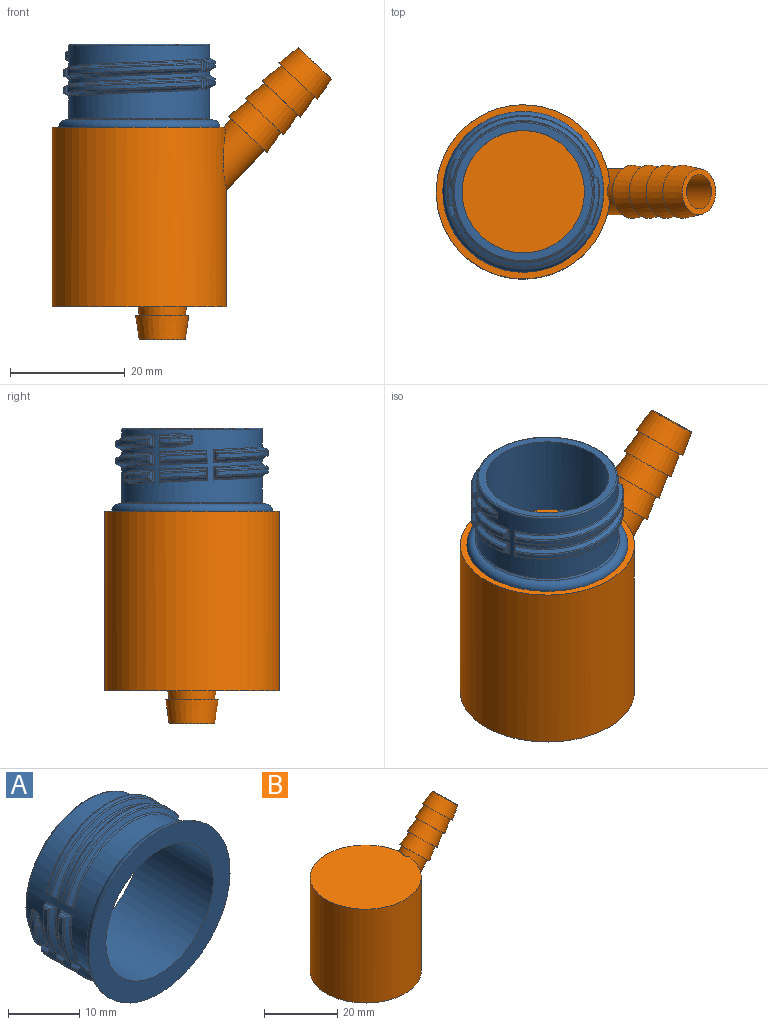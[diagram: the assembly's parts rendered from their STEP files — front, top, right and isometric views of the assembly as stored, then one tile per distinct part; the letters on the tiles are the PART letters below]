
ASSEMBLY  parts=2 mates=1
PART A: 180 faces, bbox 30.3x14.4x30.3 mm
  f0: cylinder r=0.25mm len=2.31mm, axis (0,-1,0), area 0.7mm2, adj f3,f34,f72,f106,f123,f140
  f1: bspline ~22.39x8.9mm, area 7.7mm2, adj f2,f27,f34,f151
  f2: cylinder r=0.25mm len=2.31mm, axis (0,-1,0), area 0.7mm2, adj f1,f27,f28,f32,f34,f175
  f3: bspline ~22.39x8.9mm, area 7.7mm2, adj f0,f34,f123,f124
  f4: bspline ~2.01x0.9mm, area 0.5mm2, adj f5,f31,f34,f50,f51,f139
  f5: plane 1.1x0.46mm, normal (0.06,0.88,-0.48), area 0.2mm2, adj f4,f6,f172
  f6: bspline ~1.83x0.7mm, area 0.8mm2, adj f5,f7,f35,f49,f50
  f7: bspline ~0.63x0.3mm, area 0.1mm2, adj f6,f29,f49,f105
  f8: bspline ~0.83x0.44mm, area 0.3mm2, adj f9,f10,f65,f99
  f9: bspline ~2.12x0.78mm, area 0.5mm2, adj f8,f10,f34,f60,f61,f90
  f10: bspline ~0.31x0.29mm, area 0mm2, adj f8,f9,f121
  f11: bspline ~3.72x1.35mm, area 1mm2, adj f15,f34,f93,f166
  f12: bspline ~2.11x0.63mm, area 0.5mm2, adj f13,f14,f34,f93,f153,f161
  f13: plane 1.04x0.34mm, normal (-0.43,0.89,0.14), area 0.2mm2, adj f12,f48,f114
  f14: cylinder r=0.48mm len=0.13mm, axis (0.89,0.45,-0.06), area 0mm2, adj f12,f15,f93,f114
  f15: bspline ~4.62x2.22mm, area 2.8mm2, adj f11,f14,f70,f75,f95,f114,f117,f119
  f16: bspline ~10.2x2.57mm, area 6.7mm2, adj f38,f45,f83,f86,f92,f96,f115,f149
  f17: bspline ~4.61x2.22mm, area 2.8mm2, adj f61,f62,f64,f70,f102,f119,f138,f163
  f18: bspline ~10.2x2.57mm, area 6.7mm2, adj f38,f73,f83,f86,f96,f115,f149,f170
  f19: cylinder r=13.25mm len=7.77mm, axis (0,-1,0), area 5.5mm2, adj f37,f84,f91,f176
  f20: cylinder r=13.25mm len=23.24mm, axis (0,-1,0), area 19.9mm2, adj f44,f148,f152,f167
  f21: cylinder r=13.25mm len=7.77mm, axis (0,-1,0), area 5.5mm2, adj f38,f45,f83,f170
  f22: cylinder r=13.25mm len=23.24mm, axis (0,-1,0), area 19.9mm2, adj f47,f111,f125,f126
  f23: cylinder r=13.25mm len=7.77mm, axis (0,-1,0), area 5.5mm2, adj f42,f43,f77,f81
  f24: bspline ~10.2x2.57mm, area 6.7mm2, adj f41,f97,f100,f147,f155,f159,f162,f179
  f25: bspline ~25.54x12.83mm, area 22.9mm2, adj f39,f46,f78,f108,f110,f122,f142,f171
  f26: bspline ~10.2x2.57mm, area 6.7mm2, adj f37,f91,f103,f120,f137,f156,f157,f176
  f27: bspline ~25.54x12.83mm, area 22.9mm2, adj f1,f2,f47,f111,f126,f151,f154,f175
  f28: bspline ~25.54x12.82mm, area 22.9mm2, adj f2,f32,f111,f125,f126,f151,f154,f175
  f29: bspline ~6.3x5.77mm, area 5mm2, adj f7,f36,f68,f89,f105,f139,f143,f172
  f30: bspline ~2x0.91mm, area 0.5mm2, adj f34,f52,f53,f58,f59,f136
  f31: bspline ~0.24x0.15mm, area 0mm2, adj f4,f139,f173
  f32: bspline ~22.25x8.69mm, area 7.7mm2, adj f2,f28,f34,f151
  f33: cylinder r=0.25mm len=2.31mm, axis (0,-1,0), area 0.7mm2, adj f34,f76,f94,f101,f116,f177
  f34: cylinder r=12.25mm len=24.5mm, axis (0,-1,0), area 606.8mm2, adj f0,f1,f2,f3,f4,f9,f11,f12
  f35: cylinder r=5mm len=3.78mm, axis (0,-1,0), area 2.6mm2, adj f6,f50,f53,f54,f69,f85,f105,f135
  f36: cylinder r=0.25mm len=1.21mm, axis (0,1,0), area 0.3mm2, adj f29,f79,f89,f135,f143,f165
  f37: cylinder r=0.25mm len=1.21mm, axis (0,-1,0), area 0.3mm2, adj f19,f26,f84,f98,f103,f176
  f38: cylinder r=0.25mm len=1.21mm, axis (0,-1,0), area 0.3mm2, adj f16,f18,f21,f45,f86,f170
  f39: cylinder r=0.25mm len=1.21mm, axis (0,-1,0), area 0.3mm2, adj f25,f46,f108,f132,f134,f146
  f40: cylinder r=0.25mm len=1.21mm, axis (0,1,0), area 0.3mm2, adj f112,f128,f129,f131,f160,f168
  f41: cylinder r=0.25mm len=1.21mm, axis (0,1,0), area 0.3mm2, adj f24,f82,f100,f104,f133,f162
  f42: cylinder r=0.25mm len=1.21mm, axis (0,-1,0), area 0.3mm2, adj f23,f76,f77,f81,f94,f116
  f43: cylinder r=0.25mm len=1.21mm, axis (0,1,0), area 0.3mm2, adj f23,f76,f77,f81,f94,f109
  f44: cylinder r=0.25mm len=1.21mm, axis (0,-1,0), area 0.3mm2, adj f20,f72,f106,f123,f148,f167
  f45: bspline ~8.2x1.43mm, area 2.3mm2, adj f16,f21,f38,f83
  f46: bspline ~23.45x8.91mm, area 8mm2, adj f25,f39,f134,f171
  f47: bspline ~23.45x8.91mm, area 8mm2, adj f22,f27,f111,f126
  f48: bspline ~1.77x0.58mm, area 0.8mm2, adj f13,f95,f99,f118,f161
  f49: bspline ~0.13x0.08mm, area 0mm2, adj f6,f7,f172
  f50: bspline ~0.84x0.44mm, area 0.3mm2, adj f4,f6,f35,f51
  f51: bspline ~0.3x0.29mm, area 0mm2, adj f4,f50,f85
  f52: bspline ~0.32x0.31mm, area 0mm2, adj f30,f53,f85
  f53: bspline ~0.85x0.45mm, area 0.3mm2, adj f30,f35,f52,f54
  f54: bspline ~1.77x0.58mm, area 0.8mm2, adj f35,f53,f55,f56,f136
  f55: bspline ~0.63x0.34mm, area 0.1mm2, adj f54,f56,f69,f79
  f56: bspline ~0.13x0.08mm, area 0mm2, adj f54,f55,f57
  f57: cylinder r=0.5mm len=0.41mm, axis (-0.28,0.44,-0.85), area 0.1mm2, adj f56,f58,f79,f136
  f58: cylinder r=0.48mm len=0.13mm, axis (0.22,-0.45,0.87), area 0mm2, adj f30,f57,f59,f79
  f59: bspline ~0.24x0.15mm, area 0mm2, adj f30,f58,f178
  f60: bspline ~0.24x0.14mm, area 0mm2, adj f9,f61,f138
  f61: cylinder r=0.47mm len=0.13mm, axis (-0.86,0.42,-0.29), area 0mm2, adj f9,f17,f60,f62
  f62: cylinder r=0.5mm len=0.4mm, axis (-0.89,0.45,0), area 0.1mm2, adj f17,f61,f63,f90
  f63: bspline ~0.12x0.11mm, area 0mm2, adj f62,f64,f65
  f64: bspline ~0.6x0.3mm, area 0.1mm2, adj f17,f63,f65,f102
  f65: bspline ~1.83x0.7mm, area 0.8mm2, adj f8,f63,f64,f90,f99
  f66: plane 28x28mm, normal (0,-1,0), area 259.4mm2, adj f67,f127
  f67: cylinder r=10.65mm len=21.3mm, axis (0,-1,0), area 964mm2, adj f66,f74
  f68: cylinder r=0.25mm len=2.31mm, axis (0,-1,0), area 0.7mm2, adj f29,f34,f79,f89,f173,f178
  f69: bspline ~1.21x0.73mm, area 0.4mm2, adj f35,f55,f79,f165
  f70: plane 1.8x0.59mm, normal (0.26,0,-0.97), area 0.9mm2, adj f15,f17,f119,f166
  f71: plane 1.8x0.53mm, normal (-0.5,0,-0.87), area 0.9mm2, adj f128,f129,f144,f150
  f72: bspline ~25.54x12.82mm, area 22.9mm2, adj f0,f44,f106,f124,f140,f145,f152,f167
  f73: bspline ~8.47x1.55mm, area 2.3mm2, adj f18,f34,f96,f149
  f74: plane 24x24mm, normal (0,1,0), area 96.1mm2, adj f67,f174
  f75: bspline ~1.87x0.85mm, area 0.5mm2, adj f15,f117,f119,f130
  f76: bspline ~10.2x2.57mm, area 6.7mm2, adj f33,f42,f43,f77,f109,f116,f164,f177
  f77: bspline ~8.2x1.43mm, area 2.3mm2, adj f23,f42,f43,f76
  f78: plane 1.8x0.53mm, normal (-0.5,0,-0.87), area 0.9mm2, adj f25,f110,f132,f171
  f79: bspline ~6.3x5.77mm, area 5mm2, adj f36,f55,f57,f58,f68,f69,f89,f165
  f80: bspline ~22.25x8.69mm, area 7.7mm2, adj f34,f110,f122,f132
  f81: bspline ~8.2x1.43mm, area 2.3mm2, adj f23,f42,f43,f94
  f82: bspline ~8.2x1.43mm, area 2.3mm2, adj f41,f104,f133,f179
  f83: cylinder r=0.25mm len=1.21mm, axis (0,-1,0), area 0.3mm2, adj f16,f18,f21,f45,f115,f170
  f84: bspline ~8.2x1.43mm, area 2.3mm2, adj f19,f37,f91,f98
  f85: cylinder r=0.25mm len=1.34mm, axis (0,1,0), area 0.1mm2, adj f34,f35,f51,f52
  f86: plane 1.8x0.59mm, normal (-0.26,0,0.97), area 0.9mm2, adj f16,f18,f38,f96
  f87: cylinder r=0.25mm len=2.31mm, axis (0,-1,0), area 0.7mm2, adj f34,f88,f112,f128,f129,f141
  f88: bspline ~22.25x8.69mm, area 7.7mm2, adj f34,f87,f128,f150
  f89: plane 1.8x0.43mm, normal (-0.71,0,0.71), area 0.9mm2, adj f29,f36,f68,f79
  f90: plane 1.09x0.35mm, normal (-0.44,-0.88,0.2), area 0.2mm2, adj f9,f62,f65
  f91: cylinder r=0.25mm len=1.21mm, axis (0,-1,0), area 0.3mm2, adj f19,f26,f84,f98,f137,f176
  f92: bspline ~8.37x1.52mm, area 2.3mm2, adj f16,f34,f96,f149
  f93: bspline ~0.24x0.14mm, area 0mm2, adj f11,f12,f14
  f94: bspline ~10.2x2.57mm, area 6.7mm2, adj f33,f42,f43,f81,f101,f109,f116,f164
  f95: bspline ~0.6x0.34mm, area 0.1mm2, adj f15,f48,f117,f118
  f96: cylinder r=0.25mm len=2.31mm, axis (0,-1,0), area 0.7mm2, adj f16,f18,f34,f73,f86,f92
  f97: plane 1.8x0.61mm, normal (0,0,1), area 0.9mm2, adj f24,f104,f159,f179
  f98: bspline ~10.2x2.57mm, area 6.7mm2, adj f37,f84,f91,f103,f120,f137,f157,f169
  f99: cylinder r=5mm len=3.86mm, axis (0,-1,0), area 2.6mm2, adj f8,f48,f65,f102,f117,f121,f130,f161
  f100: bspline ~8.2x1.43mm, area 2.3mm2, adj f24,f41,f133,f179
  f101: bspline ~8.47x1.56mm, area 2.3mm2, adj f33,f34,f94,f164
  f102: bspline ~1.28x0.35mm, area 0.4mm2, adj f17,f64,f99,f163
  f103: plane 1.8x0.59mm, normal (-0.26,0,0.97), area 0.9mm2, adj f26,f37,f98,f120
  f104: bspline ~10.2x2.57mm, area 6.7mm2, adj f41,f82,f97,f113,f155,f159,f162,f179
  f105: bspline ~1.19x0.71mm, area 0.4mm2, adj f7,f29,f35,f143
  f106: plane 1.8x0.53mm, normal (0.5,0,0.87), area 0.9mm2, adj f0,f44,f72,f123
  f107: torus R=12.5mm, axis (0,1,0), area 34.8mm2, adj f127,f158
  f108: plane 1.8x0.43mm, normal (0.71,0,-0.71), area 0.9mm2, adj f25,f39,f122,f132
  f109: plane 1.8x0.61mm, normal (0,0,1), area 0.9mm2, adj f43,f76,f94,f164
  f110: cylinder r=0.25mm len=2.31mm, axis (0,-1,0), area 0.7mm2, adj f25,f34,f78,f80,f132,f142
  f111: cylinder r=0.25mm len=1.21mm, axis (0,-1,0), area 0.3mm2, adj f22,f27,f28,f47,f125,f175
  f112: plane 1.8x0.43mm, normal (0.71,0,-0.71), area 0.9mm2, adj f40,f87,f128,f129
  f113: bspline ~8.47x1.56mm, area 2.3mm2, adj f34,f104,f155,f159
  f114: cylinder r=0.5mm len=0.4mm, axis (-0.9,-0.44,0), area 0.1mm2, adj f13,f14,f15,f118
  f115: plane 1.8x0.61mm, normal (0,0,-1), area 0.9mm2, adj f16,f18,f83,f149
  f116: plane 1.8x0.59mm, normal (0.26,0,-0.97), area 0.9mm2, adj f33,f42,f76,f94
  f117: bspline ~1.32x0.35mm, area 0.4mm2, adj f15,f75,f95,f99
  f118: bspline ~0.12x0.11mm, area 0mm2, adj f48,f95,f114
  f119: cylinder r=0.25mm len=1.21mm, axis (0,-1,0), area 0.3mm2, adj f15,f17,f70,f75,f130,f163
  f120: cylinder r=0.25mm len=2.31mm, axis (0,-1,0), area 0.7mm2, adj f26,f34,f98,f103,f156,f169
  f121: cylinder r=0.25mm len=1.34mm, axis (0,-1,0), area 0.1mm2, adj f10,f34,f99,f153
  f122: cylinder r=0.25mm len=2.31mm, axis (0,-1,0), area 0.7mm2, adj f25,f34,f80,f108,f132,f142
  f123: bspline ~25.54x12.83mm, area 22.9mm2, adj f0,f3,f44,f106,f124,f145,f148,f152
  f124: cylinder r=0.25mm len=2.31mm, axis (0,-1,0), area 0.7mm2, adj f3,f34,f72,f123,f140,f145
  f125: bspline ~23.6x9.12mm, area 8mm2, adj f22,f28,f111,f126
  f126: cylinder r=0.25mm len=1.21mm, axis (0,-1,0), area 0.3mm2, adj f22,f27,f28,f47,f125,f154
  f127: torus R=12.76mm, axis (0,1,0), area 183mm2, adj f66,f107
  f128: bspline ~25.54x12.83mm, area 22.9mm2, adj f40,f71,f87,f88,f112,f144,f150,f160
  f129: bspline ~25.54x12.82mm, area 22.9mm2, adj f40,f71,f87,f112,f141,f144,f150,f168
  f130: cylinder r=13.25mm len=1.63mm, axis (0,-1,0), area 1.2mm2, adj f75,f99,f119,f163
  f131: cylinder r=13.25mm len=23.24mm, axis (0,-1,0), area 19.9mm2, adj f40,f144,f160,f168
  f132: bspline ~25.54x12.82mm, area 22.9mm2, adj f39,f78,f80,f108,f110,f122,f146,f171
  f133: cylinder r=13.25mm len=7.77mm, axis (0,-1,0), area 5.5mm2, adj f41,f82,f100,f179
  f134: cylinder r=13.25mm len=23.24mm, axis (0,-1,0), area 19.9mm2, adj f39,f46,f146,f171
  f135: cylinder r=13.25mm len=3.18mm, axis (0,-1,0), area 3.1mm2, adj f35,f36,f143,f165
  f136: plane 1.06x0.44mm, normal (0,-0.89,-0.46), area 0.2mm2, adj f30,f54,f57
  f137: plane 1.8x0.61mm, normal (0,0,-1), area 0.9mm2, adj f26,f91,f98,f157
  f138: bspline ~3.75x1.35mm, area 1mm2, adj f17,f34,f60,f166
  f139: cylinder r=0.47mm len=0.13mm, axis (-0.54,-0.42,-0.73), area 0mm2, adj f4,f29,f31,f172
  f140: bspline ~22.25x8.69mm, area 7.7mm2, adj f0,f34,f72,f124
  f141: bspline ~22.25x8.69mm, area 7.7mm2, adj f34,f87,f129,f150
  f142: bspline ~22.39x8.9mm, area 7.7mm2, adj f25,f34,f110,f122
  f143: bspline ~3.47x3.42mm, area 1.3mm2, adj f29,f36,f105,f135
  f144: cylinder r=0.25mm len=1.21mm, axis (0,-1,0), area 0.3mm2, adj f71,f128,f129,f131,f160,f168
  f145: plane 1.8x0.43mm, normal (-0.71,0,0.71), area 0.9mm2, adj f72,f123,f124,f152
  f146: bspline ~23.6x9.12mm, area 8mm2, adj f39,f132,f134,f171
  f147: bspline ~8.47x1.56mm, area 2.3mm2, adj f24,f34,f155,f159
  f148: bspline ~23.45x8.91mm, area 8mm2, adj f20,f44,f123,f152
  f149: cylinder r=0.25mm len=2.31mm, axis (0,-1,0), area 0.7mm2, adj f16,f18,f34,f73,f92,f115
  f150: cylinder r=0.25mm len=2.31mm, axis (0,-1,0), area 0.7mm2, adj f34,f71,f88,f128,f129,f141
  f151: cylinder r=0.25mm len=2.31mm, axis (0,-1,0), area 0.7mm2, adj f1,f27,f28,f32,f34,f154
  f152: cylinder r=0.25mm len=1.21mm, axis (0,1,0), area 0.3mm2, adj f20,f72,f123,f145,f148,f167
  f153: bspline ~0.32x0.31mm, area 0mm2, adj f12,f121,f161
  f154: plane 1.8x0.53mm, normal (0.5,0,0.87), area 0.9mm2, adj f27,f28,f126,f151
  f155: cylinder r=0.25mm len=2.31mm, axis (0,-1,0), area 0.7mm2, adj f24,f34,f104,f113,f147,f162
  f156: bspline ~8.47x1.56mm, area 2.3mm2, adj f26,f34,f120,f157
  f157: cylinder r=0.25mm len=2.31mm, axis (0,-1,0), area 0.7mm2, adj f26,f34,f98,f137,f156,f169
  f158: torus R=12mm, axis (0,-1,0), area 0.8mm2, adj f34,f107
  f159: cylinder r=0.25mm len=2.31mm, axis (0,-1,0), area 0.7mm2, adj f24,f34,f97,f104,f113,f147
  f160: bspline ~23.45x8.91mm, area 8mm2, adj f40,f128,f131,f144
  f161: bspline ~0.86x0.45mm, area 0.3mm2, adj f12,f48,f99,f153
  f162: plane 1.8x0.59mm, normal (0.26,0,-0.97), area 0.9mm2, adj f24,f41,f104,f155
  f163: bspline ~1.9x0.85mm, area 0.5mm2, adj f17,f102,f119,f130
  f164: cylinder r=0.25mm len=2.19mm, axis (0,-1,0), area 0.7mm2, adj f34,f76,f94,f101,f109
  f165: bspline ~3.46x3.4mm, area 1.3mm2, adj f36,f69,f79,f135
  f166: cylinder r=0.25mm len=2.31mm, axis (0,-1,0), area 0.7mm2, adj f11,f15,f17,f34,f70,f138
  f167: bspline ~23.6x9.12mm, area 8mm2, adj f20,f44,f72,f152
  f168: bspline ~23.6x9.12mm, area 8mm2, adj f40,f129,f131,f144
  f169: bspline ~8.37x1.52mm, area 2.3mm2, adj f34,f98,f120,f157
  f170: bspline ~8.2x1.43mm, area 2.3mm2, adj f18,f21,f38,f83
  f171: cylinder r=0.25mm len=1.21mm, axis (0,-1,0), area 0.3mm2, adj f25,f46,f78,f132,f134,f146
  f172: cylinder r=0.5mm len=0.41mm, axis (-0.28,-0.45,-0.85), area 0.1mm2, adj f5,f29,f49,f139
  f173: bspline ~4.89x4.47mm, area 1.8mm2, adj f29,f31,f34,f68
  f174: torus R=12mm, axis (0,1,0), area 30mm2, adj f34,f74
  f175: plane 1.8x0.43mm, normal (-0.71,0,0.71), area 0.9mm2, adj f2,f27,f28,f111
  f176: bspline ~8.2x1.43mm, area 2.3mm2, adj f19,f26,f37,f91
  f177: bspline ~8.26x1.51mm, area 2.3mm2, adj f33,f34,f76
  f178: bspline ~4.88x4.47mm, area 1.8mm2, adj f34,f59,f68,f79
  f179: cylinder r=0.25mm len=1.21mm, axis (0,-1,0), area 0.3mm2, adj f24,f82,f97,f100,f104,f133
PART B: 98 faces, bbox 49.5x31.2x51.7 mm
  f0: bspline ~1.77x1.26mm, area 0.5mm2, adj f2,f3,f6,f8
  f1: bspline ~1.75x1.25mm, area 0.5mm2, adj f4,f5,f6,f10
  f2: plane 1.51x0.95mm, normal (-0.18,0.43,-0.89), area 0.7mm2, adj f0,f7,f13
  f3: bspline ~0.23x0.18mm, area 0mm2, adj f0,f6,f13,f14
  f4: plane 1.51x0.95mm, normal (-0.24,0.41,0.88), area 0.7mm2, adj f1,f11,f16
  f5: bspline ~0.23x0.17mm, area 0mm2, adj f1,f6,f16,f17
  f6: cylinder r=5mm len=2.26mm, axis (0,0,1), area 2.2mm2, adj f0,f1,f3,f5,f9,f14,f17,f58
  f7: bspline ~1.55x0.4mm, area 0.4mm2, adj f2,f8,f12,f53
  f8: bspline ~0.48x0.39mm, area 0.1mm2, adj f0,f7,f9,f53
  f9: cylinder r=0.25mm len=1mm, axis (0,0,1), area 0.2mm2, adj f6,f8,f10,f53
  f10: bspline ~0.46x0.41mm, area 0.1mm2, adj f1,f9,f11,f53
  f11: bspline ~1.56x0.52mm, area 0.4mm2, adj f4,f10,f15,f53
  f12: bspline ~0.23x0.17mm, area 0mm2, adj f7,f13,f45,f53
  f13: cylinder r=1.25mm len=0.73mm, axis (0.08,-0.89,-0.45), area 0.1mm2, adj f2,f3,f12,f44
  f14: bspline ~0.49x0.27mm, area 0.1mm2, adj f3,f6,f43,f44
  f15: bspline ~0.24x0.18mm, area 0mm2, adj f11,f16,f48,f53
  f16: cylinder r=1.19mm len=0.73mm, axis (-0.09,0.89,-0.44), area 0.1mm2, adj f4,f5,f15,f47
  f17: bspline ~0.47x0.27mm, area 0.1mm2, adj f5,f6,f46,f47
  f18: plane 6.87x3.87mm, normal (0,0,-1), area 3.9mm2, adj f19,f20
  f19: cylinder r=2.18mm len=17.94mm, axis (0.69,0,0.73), area 220.4mm2, adj f18,f66,f67
  f20: cylinder r=3mm len=20mm, axis (0,0,-1), area 377mm2, adj f18,f21,f67
  f21: plane 8x8mm, normal (0,0,-1), area 22mm2, adj f20,f22
  f22: cone r=4mm half-angle=8.4deg, axis (0,0,1), area 116.4mm2, adj f21,f23
  f23: plane 9.25x9.25mm, normal (0,0,1), area 16.9mm2, adj f22,f24
  f24: cone r=4.62mm half-angle=8.4deg, axis (0,0,1), area 116.4mm2, adj f23,f25
  f25: plane 9.25x9.25mm, normal (0,0,1), area 16.9mm2, adj f24,f30
  f26: cylinder r=4mm len=8mm, axis (0,0,-1), area 75.4mm2, adj f27,f65
  f27: plane 9.25x9.25mm, normal (0,0,1), area 16.9mm2, adj f26,f28
  f28: cone r=4.62mm half-angle=8.4deg, axis (0,0,1), area 116.4mm2, adj f27,f29
  f29: plane 9.25x9.25mm, normal (0,0,1), area 16.9mm2, adj f28,f30
  f30: cone r=4.62mm half-angle=8.4deg, axis (0,0,1), area 116.4mm2, adj f25,f29
  f31: cylinder r=3mm len=22.71mm, axis (0.69,0,0.73), area 426.8mm2, adj f32,f66
  f32: plane 8x5.81mm, normal (0.69,0,0.73), area 22mm2, adj f31,f33
  f33: cone r=4mm half-angle=8.4deg, axis (-0.69,0,-0.73), area 116.4mm2, adj f32,f34
  f34: plane 9.25x6.72mm, normal (-0.69,0,-0.73), area 16.9mm2, adj f33,f35
  f35: cone r=4.62mm half-angle=8.4deg, axis (-0.69,0,-0.73), area 116.4mm2, adj f34,f36
  f36: plane 9.25x6.72mm, normal (-0.69,0,-0.73), area 16.9mm2, adj f35,f41
  f37: cylinder r=4mm len=12.51mm, axis (0.69,0,0.73), area 147.2mm2, adj f38,f42,f64
  f38: plane 9.25x6.72mm, normal (-0.69,0,-0.73), area 16.9mm2, adj f37,f39
  f39: cone r=4.62mm half-angle=8.4deg, axis (-0.69,0,-0.73), area 116.4mm2, adj f38,f40
  f40: plane 9.25x6.72mm, normal (-0.69,0,-0.73), area 16.9mm2, adj f39,f41
  f41: cone r=4.62mm half-angle=8.4deg, axis (-0.69,0,-0.73), area 116.4mm2, adj f36,f40
  f42: plane 30.95x30.87mm, normal (0,0,1), area 719.8mm2, adj f37,f64
  f43: bspline ~13.96x9.39mm, area 4.6mm2, adj f14,f44,f58,f96
  f44: bspline ~14.81x12.8mm, area 14.2mm2, adj f13,f14,f43,f45,f95
  f45: bspline ~14.78x10.56mm, area 5.1mm2, adj f12,f44,f53,f94
  f46: bspline ~13.95x9.39mm, area 4.6mm2, adj f17,f47,f58,f97
  f47: bspline ~14.82x12.81mm, area 14.2mm2, adj f16,f17,f46,f48,f91
  f48: bspline ~14.77x10.56mm, area 5.1mm2, adj f15,f47,f53,f88
  f49: bspline ~25.86x16.1mm, area 11.1mm2, adj f50,f58,f92,f96
  f50: bspline ~27.9x18.58mm, area 33.7mm2, adj f49,f51,f89,f95
  f51: bspline ~27.52x15.44mm, area 11.9mm2, adj f50,f53,f86,f94
  f52: plane 30.3x30.3mm, normal (0,0,-1), area 127.1mm2, adj f53,f64
  f53: cylinder r=13.75mm len=27.5mm, axis (0,0,-1), area 526.5mm2, adj f7,f8,f9,f10,f11,f12,f15,f45
  f54: cylinder r=13.75mm len=27.5mm, axis (0,0,-1), area 381.3mm2, adj f53,f57,f59,f79,f80,f81,f82,f83
  f55: bspline ~25.78x12.89mm, area 11.1mm2, adj f56,f58,f93,f97
  f56: bspline ~27.91x18.59mm, area 33.7mm2, adj f55,f57,f90,f91
  f57: bspline ~27.52x15.46mm, area 11.9mm2, adj f54,f56,f87,f88
  f58: cylinder r=12.75mm len=25.5mm, axis (0,0,1), area 87.9mm2, adj f6,f43,f46,f49,f55,f74,f92,f93
  f59: plane 27.5x27.5mm, normal (0,0,-1), area 229.2mm2, adj f54,f60
  f60: cylinder r=10.78mm len=21.55mm, axis (0,0,-1), area 88mm2, adj f59,f61
  f61: cone r=10.78mm half-angle=7.6deg, axis (0,0,-1), area 68.1mm2, adj f60,f62
  f62: cone r=10.91mm half-angle=49.4deg, axis (0,0,-1), area 98.9mm2, adj f61,f63
  f63: cylinder r=9.75mm len=19.5mm, axis (0,0,1), area 79.6mm2, adj f62,f65
  f64: cylinder r=15.15mm len=31.3mm, axis (0,0,-1), area 2907mm2, adj f37,f42,f52
  f65: plane 19.5x19.5mm, normal (0,0,-1), area 248.4mm2, adj f26,f63
  f66: cylinder r=15.15mm len=8.73mm, axis (0,0,-1), area 19.6mm2, adj f19,f31
  f67: plane 6.87x3.87mm, normal (0,0,-1), area 3.9mm2, adj f19,f20
  f68: bspline ~0.23x0.2mm, area 0mm2, adj f71,f74,f75,f76
  f69: bspline ~0.23x0.18mm, area 0mm2, adj f72,f74,f77,f78
  f70: plane 1.49x1.25mm, normal (0.3,-0.35,0.89), area 0.7mm2, adj f71,f76,f80
  f71: bspline ~1.83x1.12mm, area 0.5mm2, adj f68,f70,f74,f81
  f72: bspline ~1.84x1.12mm, area 0.5mm2, adj f69,f73,f74,f83
  f73: plane 1.49x1.25mm, normal (0.26,-0.4,-0.88), area 0.7mm2, adj f72,f77,f84
  f74: cylinder r=5mm len=2.22mm, axis (0,0,-1), area 2.2mm2, adj f58,f68,f69,f71,f72,f75,f78,f82
  f75: bspline ~0.43x0.41mm, area 0.1mm2, adj f68,f74,f90,f93
  f76: cylinder r=1.25mm len=0.69mm, axis (-0.77,0.46,0.45), area 0.1mm2, adj f68,f70,f79,f90
  f77: cylinder r=1.19mm len=0.69mm, axis (0.77,-0.47,0.44), area 0.1mm2, adj f69,f73,f85,f89
  f78: bspline ~0.41x0.41mm, area 0.1mm2, adj f69,f74,f89,f92
  f79: bspline ~0.23x0.21mm, area 0mm2, adj f54,f76,f80,f87
  f80: bspline ~1.32x1.03mm, area 0.4mm2, adj f54,f70,f79,f81
  f81: bspline ~0.41x0.39mm, area 0.1mm2, adj f54,f71,f80,f82
  f82: cylinder r=0.25mm len=1.01mm, axis (0,0,1), area 0.2mm2, adj f54,f74,f81,f83
  f83: bspline ~0.41x0.4mm, area 0.1mm2, adj f54,f72,f82,f84
  f84: bspline ~1.32x1.04mm, area 0.4mm2, adj f54,f73,f83,f85
  f85: bspline ~0.24x0.22mm, area 0mm2, adj f54,f77,f84,f86
  f86: bspline ~24.35x15.41mm, area 9.3mm2, adj f51,f54,f85,f89
  f87: bspline ~24.34x15.42mm, area 9.3mm2, adj f54,f57,f79,f90
  f88: bspline ~27.53x15.66mm, area 11.9mm2, adj f48,f54,f57,f91
  f89: bspline ~25.56x17.69mm, area 26.2mm2, adj f50,f77,f78,f86,f92
  f90: bspline ~25.57x17.69mm, area 26.2mm2, adj f56,f75,f76,f87,f93
  f91: bspline ~27.91x18.59mm, area 33.7mm2, adj f47,f56,f88,f97
  f92: bspline ~22.54x14.68mm, area 8.5mm2, adj f49,f58,f78,f89
  f93: bspline ~22.53x14.7mm, area 8.6mm2, adj f55,f58,f75,f90
  f94: bspline ~27.53x15.68mm, area 11.9mm2, adj f45,f51,f53,f95
  f95: bspline ~27.9x18.58mm, area 33.7mm2, adj f44,f50,f94,f96
  f96: bspline ~25.81x14.75mm, area 11.1mm2, adj f43,f49,f58,f95
  f97: bspline ~25.78x12.89mm, area 11.1mm2, adj f46,f55,f58,f91
PLACE A rot(axis=(1,0,0),90deg) t=(-13.04,26.3,-140.25)mm
PLACE B t=(-13.04,26.3,46.34)mm
MATE planar A.f34 <-> B.f53  axis (0,0,-1) through (-13.04,26.3,63.34)mm
